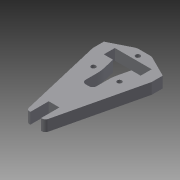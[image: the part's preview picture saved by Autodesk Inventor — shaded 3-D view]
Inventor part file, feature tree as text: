
AUTODESK INVENTOR PART (.ipt)
format: ipt  version: 2015 (Build 190159000, 159)  size: 165,376 bytes
history: native  units: mm
features: extrude x2, sketch x1
ambient origin geometry x8: Origin, YZ Plane, XZ Plane, XY Plane, X Axis, Y Axis, Z Axis, Center Point
bodies: Body1 (feature_tree)
feature tree (3):
  extrude  "Extrusion7"  Depth=20.0mm
  extrude  "Extrusion8"  Depth=5.8mm
  sketch  "Sketch1"  dims[d59=15.0mm d69=20.0mm d88=5.8mm d95=2.0mm d96=2.0mm d97=10.0mm d98=10.0mm d109=43.0mm d112=2.5mm d113=2.5mm d114=2.5mm d123=32.0mm d126=8.0mm d127=4.0mm d130=6.0mm d131=0.0mm d132=6.0mm d134=6.0mm d135=6.0mm d142=6.0mm d143=0.0mm d144=16.0mm d145=35.5mm d148=5.0mm d149=5.0mm d153=6.0mm d155=6.0mm d156=135.0deg d157=25.0mm d160=6.0mm d161=20.0mm d162=2.0mm d163=2.0mm]
